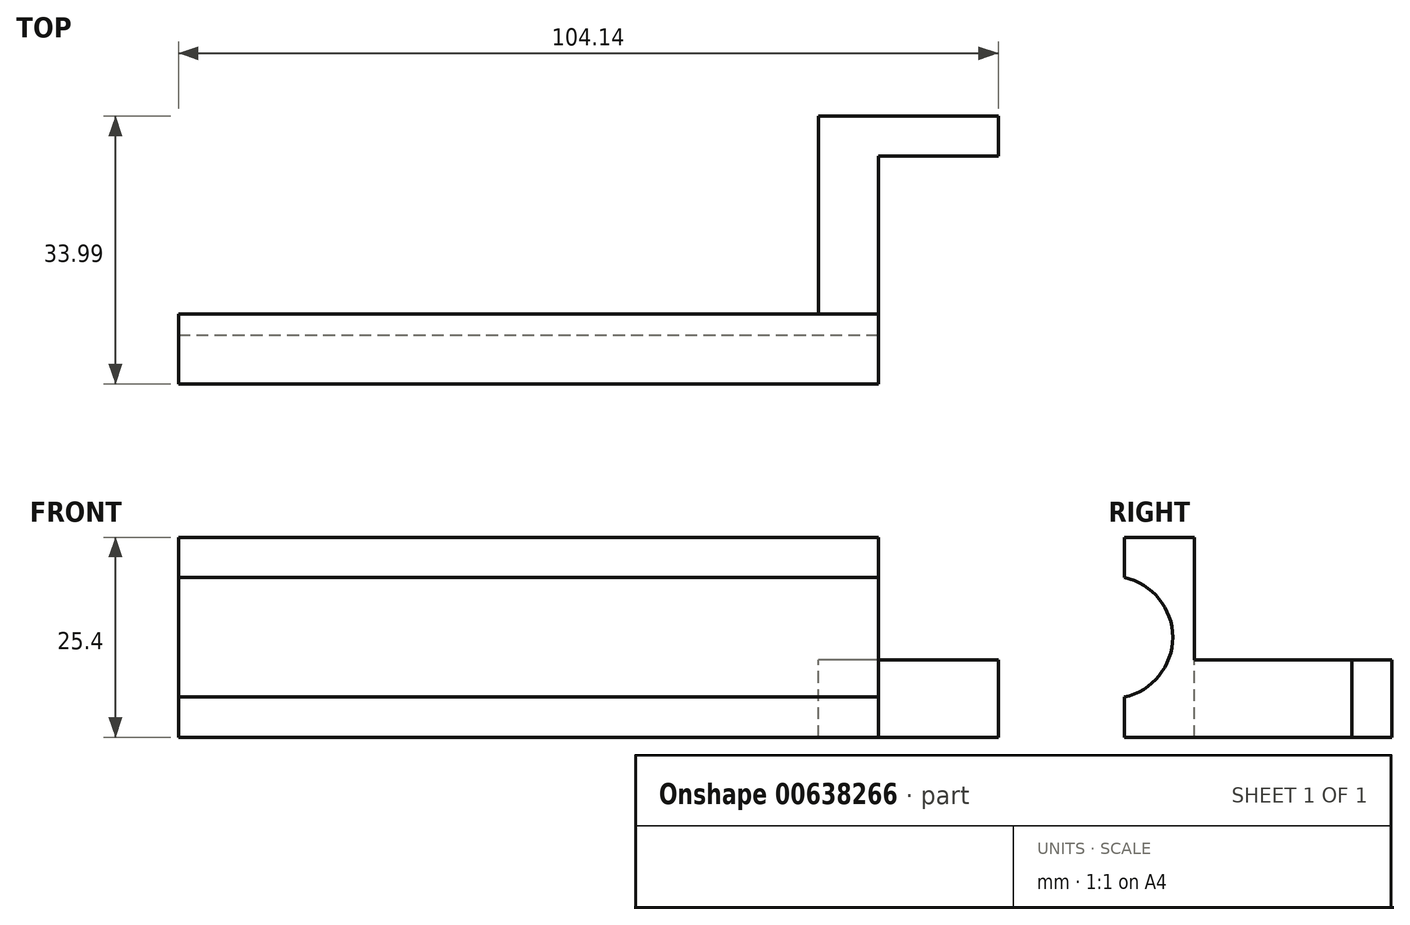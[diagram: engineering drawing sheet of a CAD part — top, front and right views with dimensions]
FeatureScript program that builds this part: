
annotation { "Feature Type Name" : "Feature", "Feature Type Description" : "" }
export const myFeature = defineFeature(function(context is Context, id is Id, definition is map)
    precondition{}
    {
        {
            var Q0;
            Q0=qCreatedBy(makeId("Front.planeOp"),FACE);
            var sketch = newSketch(context, id + "F0", { "sketchPlane" : qUnion([Q0])});
            skLineSegment(sketch, "E0.bottom", {"start": v(0, 0) * mm, "end": v(-88.9, 0) * mm});
            skLineSegment(sketch, "E0.top", {"start": v(0, 25.4) * mm, "end": v(-88.9, 25.4) * mm});
            skLineSegment(sketch, "E0.left", {"start": v(0, 0) * mm, "end": v(0, 25.4) * mm});
            skLineSegment(sketch, "E0.right", {"start": v(-88.9, 0) * mm, "end": v(-88.9, 25.4) * mm});
            skSolve(sketch);
        }
        {
            var Q0;
            Q0=qSketchRegion(id+"F0",true);
            extrude(context, id + "F1", {"entities" : qUnion([Q0]), "depth" : 8.9 * mm, "offsetDistance" : 25.4 * mm});
        }
        {
            var Q0;
            Q0=makeQuery(id+"F1.opExtrude","SWEPT_FACE",FACE,{"disambiguationData":[OSD([sQuery(id+"F0.wireOp",EDGE,"E0.right")])]});
            var sketch = newSketch(context, id + "F2", { "sketchPlane" : qUnion([Q0])});
            skCircle(sketch, "E1", {"center": v(10.48, 12.7) * mm, "radius": 7.75 * mm});
            skSolve(sketch);
        }
        {
            var Q0;
            Q0=qSketchRegion(id+"F2",true);
            extrude(context, id + "F3", {"entities" : qUnion([Q0]), "operationType" : NewBodyOperationType.REMOVE, "endBound" : BoundingType.THROUGH_ALL, "oppositeDirection" : true, "depth" : 25.4 * mm, "offsetDistance" : 25.4 * mm});
        }
        {
            var Q0;
            Q0=makeQuery(id+"F1.opExtrude","CAP_FACE",FACE,{"disambiguationData":[OSD([sQuery(id+"F0.wireOp",EDGE,"E0.bottom"),sQuery(id+"F0.wireOp",EDGE,"E0.top"),sQuery(id+"F0.wireOp",EDGE,"E0.left"),sQuery(id+"F0.wireOp",EDGE,"E0.right")])],"isStart":true});
            var sketch = newSketch(context, id + "F4", { "sketchPlane" : qUnion([Q0])});
            skLineSegment(sketch, "E2.bottom", {"start": v(0, 0) * mm, "end": v(7.62, 0) * mm});
            skLineSegment(sketch, "E2.top", {"start": v(0, 9.86) * mm, "end": v(7.62, 9.86) * mm});
            skLineSegment(sketch, "E2.left", {"start": v(0, 0) * mm, "end": v(0, 9.86) * mm});
            skLineSegment(sketch, "E2.right", {"start": v(7.62, 0) * mm, "end": v(7.62, 9.86) * mm});
            skSolve(sketch);
        }
        {
            var Q0;
            Q0=qSketchRegion(id+"F4",true);
            extrude(context, id + "F5", {"entities" : qUnion([Q0]), "operationType" : NewBodyOperationType.ADD, "depth" : 25.1 * mm, "offsetDistance" : 25.4 * mm});
        }
        {
            var Q0;
            Q0=makeQuery(id+"F5.boolean.opBoolean","MERGE",FACE,{"derivedFrom":[makeQuery(id+"F1.opExtrude","SWEPT_FACE",FACE,{"disambiguationData":[OSD([sQuery(id+"F0.wireOp",EDGE,"E0.left")])]}),makeQuery(id+"F5.opExtrude","SWEPT_FACE",FACE,{"disambiguationData":[OSD([sQuery(id+"F4.wireOp",EDGE,"E2.left")])]})]});
            var sketch = newSketch(context, id + "F6", { "sketchPlane" : qUnion([Q0])});
            skLineSegment(sketch, "E3.bottom", {"start": v(25.1, 9.86) * mm, "end": v(20.02, 9.86) * mm});
            skLineSegment(sketch, "E3.top", {"start": v(25.1, 0) * mm, "end": v(20.02, 0) * mm});
            skLineSegment(sketch, "E3.left", {"start": v(25.1, 9.86) * mm, "end": v(25.1, 0) * mm});
            skLineSegment(sketch, "E3.right", {"start": v(20.02, 9.86) * mm, "end": v(20.02, 0) * mm});
            skSolve(sketch);
        }
        {
            var Q0;
            Q0=qSketchRegion(id+"F6",true);
            extrude(context, id + "F7", {"entities" : qUnion([Q0]), "operationType" : NewBodyOperationType.ADD, "depth" : 15.24 * mm, "offsetDistance" : 25.4 * mm});
        }
    });
